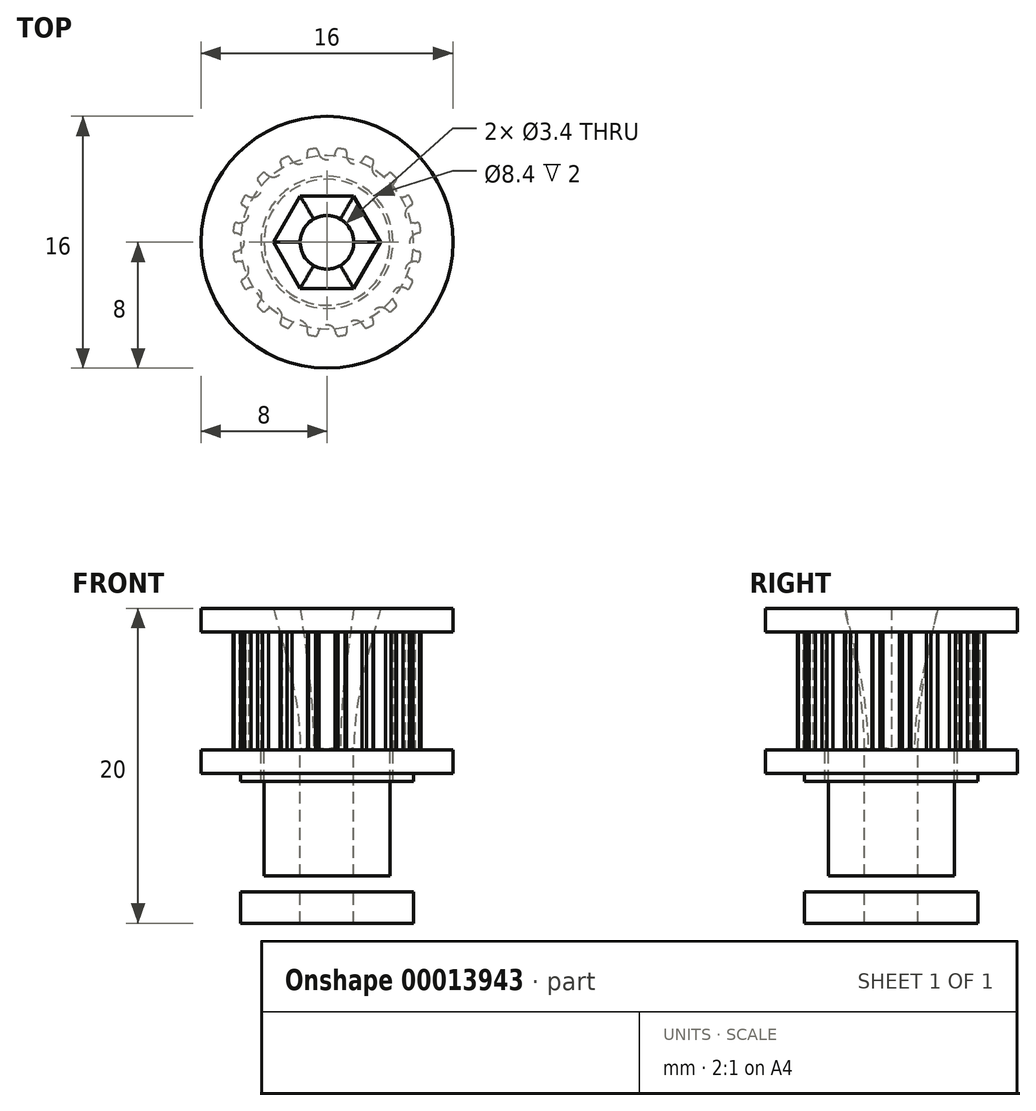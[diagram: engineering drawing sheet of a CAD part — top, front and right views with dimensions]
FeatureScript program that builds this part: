
annotation { "Feature Type Name" : "Feature", "Feature Type Description" : "" }
export const myFeature = defineFeature(function(context is Context, id is Id, definition is map)
    precondition{}
    {
        {
            var Q0;
            Q0=qCreatedBy(makeId("Top.planeOp"),FACE);
            var sketch = newSketch(context, id + "F0", { "sketchPlane" : qUnion([Q0])});
            skLineSegment(sketch, "E0", {"start": v(-19.17, 17.78) * mm, "end": v(-18.17, 17.78) * mm});
            skLineSegment(sketch, "E1", {"start": v(-18.17, 17.78) * mm, "end": v(-18.17, 18.4) * mm});
            skArc(sketch, "E2", {"start": v(-18.67, 18.85) * mm, "mid": v(-18.88, 19.07) * mm, "end": v(-19.17, 19.16) * mm});
            skArc(sketch, "E3", {"start": v(-18.58, 18.54) * mm, "mid": v(-18.61, 18.7) * mm, "end": v(-18.67, 18.85) * mm});
            skArc(sketch, "E4", {"start": v(-18.58, 18.54) * mm, "mid": v(-18.53, 18.44) * mm, "end": v(-18.43, 18.4) * mm});
            skLineSegment(sketch, "E5", {"start": v(-18.43, 18.4) * mm, "end": v(-18.17, 18.4) * mm});
            skArc(sketch, "E6.0.MirrorCS", {"start": v(-19.67, 18.85) * mm, "mid": v(-19.47, 19.07) * mm, "end": v(-19.17, 19.16) * mm});
            skArc(sketch, "E7.0.MirrorCS", {"start": v(-19.76, 18.54) * mm, "mid": v(-19.73, 18.7) * mm, "end": v(-19.67, 18.85) * mm});
            skArc(sketch, "E8.0.MirrorCS", {"start": v(-19.76, 18.54) * mm, "mid": v(-19.81, 18.44) * mm, "end": v(-19.91, 18.4) * mm});
            skLineSegment(sketch, "E9.0.MirrorCS", {"start": v(-19.91, 18.4) * mm, "end": v(-20.17, 18.4) * mm});
            skLineSegment(sketch, "E10.0.MirrorCS", {"start": v(-20.17, 17.78) * mm, "end": v(-20.17, 18.4) * mm});
            skLineSegment(sketch, "E11.0.MirrorCS", {"start": v(-19.17, 17.78) * mm, "end": v(-20.17, 17.78) * mm});
            skLineSegment(sketch, "E12.direction1", {"start": v(-20.17, 17.78) * mm, "end": v(-18.17, 17.78) * mm, "construction": true});
            skLineSegment(sketch, "E13", {"start": v(-20.17, 18.15) * mm, "end": v(-18.17, 18.15) * mm, "construction": true});
            skPoint(sketch, "E14", {"position": v(0, -5.25) * mm});
            skArc(sketch, "E15", {"start": v(0.51, -5.6) * mm, "mid": v(0, -5.25) * mm, "end": v(-0.51, -5.6) * mm});
            skArc(sketch, "E16", {"start": v(-0.51, -5.6) * mm, "mid": v(-0.56, -5.71) * mm, "end": v(-0.59, -5.83) * mm});
            skArc(sketch, "E17", {"start": v(0.59, -5.83) * mm, "mid": v(0.56, -5.71) * mm, "end": v(0.51, -5.6) * mm});
            skArc(sketch, "E18", {"start": v(0.72, -5.96) * mm, "mid": v(0.94, -5.93) * mm, "end": v(1.16, -5.89) * mm});
            skArc(sketch, "E19", {"start": v(0.59, -5.83) * mm, "mid": v(0.66, -5.94) * mm, "end": v(0.8, -5.95) * mm});
            skArc(sketch, "E20", {"start": v(-0.59, -5.83) * mm, "mid": v(-0.66, -5.94) * mm, "end": v(-0.8, -5.95) * mm});
            skArc(sketch, "E21.1.0", {"start": v(2.22, -5.16) * mm, "mid": v(1.62, -5) * mm, "end": v(1.24, -5.48) * mm});
            skPoint(sketch, "E21.1.1", {"position": v(1.62, -5) * mm});
            skArc(sketch, "E21.1.2", {"start": v(1.24, -5.48) * mm, "mid": v(1.23, -5.6) * mm, "end": v(1.24, -5.73) * mm});
            skArc(sketch, "E21.1.3", {"start": v(2.36, -5.37) * mm, "mid": v(2.47, -5.44) * mm, "end": v(2.6, -5.41) * mm});
            skArc(sketch, "E21.1.4", {"start": v(1.24, -5.73) * mm, "mid": v(1.2, -5.85) * mm, "end": v(1.08, -5.9) * mm});
            skArc(sketch, "E21.1.5", {"start": v(2.36, -5.37) * mm, "mid": v(2.3, -5.26) * mm, "end": v(2.22, -5.16) * mm});
            skArc(sketch, "E22.3.2.0", {"start": v(3.7, -4.22) * mm, "mid": v(3.09, -4.25) * mm, "end": v(2.87, -4.83) * mm});
            skPoint(sketch, "E22.4.2.0", {"position": v(3.09, -4.25) * mm});
            skArc(sketch, "E22.5.2.0", {"start": v(2.87, -4.83) * mm, "mid": v(2.9, -4.95) * mm, "end": v(2.95, -5.07) * mm});
            skArc(sketch, "E22.9.2.0", {"start": v(3.9, -4.37) * mm, "mid": v(4.03, -4.41) * mm, "end": v(4.14, -4.35) * mm});
            skArc(sketch, "E22.13.2.0", {"start": v(2.95, -5.07) * mm, "mid": v(2.95, -5.2) * mm, "end": v(2.85, -5.28) * mm});
            skArc(sketch, "E22.17.2.0", {"start": v(3.9, -4.37) * mm, "mid": v(3.81, -4.3) * mm, "end": v(3.7, -4.22) * mm});
            skArc(sketch, "E22.3.3.0", {"start": v(4.83, -2.87) * mm, "mid": v(4.25, -3.09) * mm, "end": v(4.22, -3.7) * mm});
            skPoint(sketch, "E22.4.3.0", {"position": v(4.25, -3.09) * mm});
            skArc(sketch, "E22.5.3.0", {"start": v(4.22, -3.7) * mm, "mid": v(4.3, -3.81) * mm, "end": v(4.37, -3.9) * mm});
            skArc(sketch, "E22.9.3.0", {"start": v(5.07, -2.95) * mm, "mid": v(5.2, -2.95) * mm, "end": v(5.28, -2.85) * mm});
            skArc(sketch, "E22.13.3.0", {"start": v(4.37, -3.9) * mm, "mid": v(4.41, -4.03) * mm, "end": v(4.35, -4.14) * mm});
            skArc(sketch, "E22.17.3.0", {"start": v(5.07, -2.95) * mm, "mid": v(4.95, -2.9) * mm, "end": v(4.83, -2.87) * mm});
            skArc(sketch, "E22.3.4.0", {"start": v(5.48, -1.24) * mm, "mid": v(5, -1.62) * mm, "end": v(5.16, -2.22) * mm});
            skPoint(sketch, "E22.4.4.0", {"position": v(5, -1.62) * mm});
            skArc(sketch, "E22.5.4.0", {"start": v(5.16, -2.22) * mm, "mid": v(5.26, -2.3) * mm, "end": v(5.37, -2.36) * mm});
            skArc(sketch, "E22.9.4.0", {"start": v(5.73, -1.24) * mm, "mid": v(5.85, -1.2) * mm, "end": v(5.9, -1.08) * mm});
            skArc(sketch, "E22.13.4.0", {"start": v(5.37, -2.36) * mm, "mid": v(5.44, -2.47) * mm, "end": v(5.41, -2.6) * mm});
            skArc(sketch, "E22.17.4.0", {"start": v(5.73, -1.24) * mm, "mid": v(5.6, -1.23) * mm, "end": v(5.48, -1.24) * mm});
            skArc(sketch, "E22.3.5.0", {"start": v(5.6, 0.51) * mm, "mid": v(5.25, 0) * mm, "end": v(5.6, -0.51) * mm});
            skPoint(sketch, "E22.4.5.0", {"position": v(5.25, 0) * mm});
            skArc(sketch, "E22.5.5.0", {"start": v(5.6, -0.51) * mm, "mid": v(5.71, -0.56) * mm, "end": v(5.83, -0.59) * mm});
            skArc(sketch, "E22.9.5.0", {"start": v(5.83, 0.59) * mm, "mid": v(5.94, 0.66) * mm, "end": v(5.95, 0.8) * mm});
            skArc(sketch, "E22.13.5.0", {"start": v(5.83, -0.59) * mm, "mid": v(5.94, -0.66) * mm, "end": v(5.95, -0.8) * mm});
            skArc(sketch, "E22.17.5.0", {"start": v(5.83, 0.59) * mm, "mid": v(5.71, 0.56) * mm, "end": v(5.6, 0.51) * mm});
            skArc(sketch, "E22.3.6.0", {"start": v(5.16, 2.22) * mm, "mid": v(5, 1.62) * mm, "end": v(5.48, 1.24) * mm});
            skPoint(sketch, "E22.4.6.0", {"position": v(5, 1.62) * mm});
            skArc(sketch, "E22.5.6.0", {"start": v(5.48, 1.24) * mm, "mid": v(5.6, 1.23) * mm, "end": v(5.73, 1.24) * mm});
            skArc(sketch, "E22.9.6.0", {"start": v(5.37, 2.36) * mm, "mid": v(5.44, 2.47) * mm, "end": v(5.41, 2.6) * mm});
            skArc(sketch, "E22.13.6.0", {"start": v(5.73, 1.24) * mm, "mid": v(5.85, 1.2) * mm, "end": v(5.9, 1.08) * mm});
            skArc(sketch, "E22.17.6.0", {"start": v(5.37, 2.36) * mm, "mid": v(5.26, 2.3) * mm, "end": v(5.16, 2.22) * mm});
            skArc(sketch, "E22.3.7.0", {"start": v(4.22, 3.7) * mm, "mid": v(4.25, 3.09) * mm, "end": v(4.83, 2.87) * mm});
            skPoint(sketch, "E22.4.7.0", {"position": v(4.25, 3.09) * mm});
            skArc(sketch, "E22.5.7.0", {"start": v(4.83, 2.87) * mm, "mid": v(4.95, 2.9) * mm, "end": v(5.07, 2.95) * mm});
            skArc(sketch, "E22.9.7.0", {"start": v(4.37, 3.9) * mm, "mid": v(4.41, 4.03) * mm, "end": v(4.35, 4.14) * mm});
            skArc(sketch, "E22.13.7.0", {"start": v(5.07, 2.95) * mm, "mid": v(5.2, 2.95) * mm, "end": v(5.28, 2.85) * mm});
            skArc(sketch, "E22.17.7.0", {"start": v(4.37, 3.9) * mm, "mid": v(4.3, 3.81) * mm, "end": v(4.22, 3.7) * mm});
            skArc(sketch, "E22.3.8.0", {"start": v(2.87, 4.83) * mm, "mid": v(3.09, 4.25) * mm, "end": v(3.7, 4.22) * mm});
            skPoint(sketch, "E22.4.8.0", {"position": v(3.09, 4.25) * mm});
            skArc(sketch, "E22.5.8.0", {"start": v(3.7, 4.22) * mm, "mid": v(3.81, 4.3) * mm, "end": v(3.9, 4.37) * mm});
            skArc(sketch, "E22.9.8.0", {"start": v(2.95, 5.07) * mm, "mid": v(2.95, 5.2) * mm, "end": v(2.85, 5.28) * mm});
            skArc(sketch, "E22.13.8.0", {"start": v(3.9, 4.37) * mm, "mid": v(4.03, 4.41) * mm, "end": v(4.14, 4.35) * mm});
            skArc(sketch, "E22.17.8.0", {"start": v(2.95, 5.07) * mm, "mid": v(2.9, 4.95) * mm, "end": v(2.87, 4.83) * mm});
            skArc(sketch, "E22.3.9.0", {"start": v(1.24, 5.48) * mm, "mid": v(1.62, 5) * mm, "end": v(2.22, 5.16) * mm});
            skPoint(sketch, "E22.4.9.0", {"position": v(1.62, 5) * mm});
            skArc(sketch, "E22.5.9.0", {"start": v(2.22, 5.16) * mm, "mid": v(2.3, 5.26) * mm, "end": v(2.36, 5.37) * mm});
            skArc(sketch, "E22.9.9.0", {"start": v(1.24, 5.73) * mm, "mid": v(1.2, 5.85) * mm, "end": v(1.08, 5.9) * mm});
            skArc(sketch, "E22.13.9.0", {"start": v(2.36, 5.37) * mm, "mid": v(2.47, 5.44) * mm, "end": v(2.6, 5.41) * mm});
            skArc(sketch, "E22.17.9.0", {"start": v(1.24, 5.73) * mm, "mid": v(1.23, 5.6) * mm, "end": v(1.24, 5.48) * mm});
            skArc(sketch, "E22.3.10.0", {"start": v(-0.51, 5.6) * mm, "mid": v(0, 5.25) * mm, "end": v(0.51, 5.6) * mm});
            skPoint(sketch, "E22.4.10.0", {"position": v(0, 5.25) * mm});
            skArc(sketch, "E22.5.10.0", {"start": v(0.51, 5.6) * mm, "mid": v(0.56, 5.71) * mm, "end": v(0.59, 5.83) * mm});
            skArc(sketch, "E22.9.10.0", {"start": v(-0.59, 5.83) * mm, "mid": v(-0.66, 5.94) * mm, "end": v(-0.8, 5.95) * mm});
            skArc(sketch, "E22.13.10.0", {"start": v(0.59, 5.83) * mm, "mid": v(0.66, 5.94) * mm, "end": v(0.8, 5.95) * mm});
            skArc(sketch, "E22.17.10.0", {"start": v(-0.59, 5.83) * mm, "mid": v(-0.56, 5.71) * mm, "end": v(-0.51, 5.6) * mm});
            skArc(sketch, "E22.3.11.0", {"start": v(-2.22, 5.16) * mm, "mid": v(-1.62, 5) * mm, "end": v(-1.24, 5.48) * mm});
            skPoint(sketch, "E22.4.11.0", {"position": v(-1.62, 5) * mm});
            skArc(sketch, "E22.5.11.0", {"start": v(-1.24, 5.48) * mm, "mid": v(-1.23, 5.6) * mm, "end": v(-1.24, 5.73) * mm});
            skArc(sketch, "E22.9.11.0", {"start": v(-2.36, 5.37) * mm, "mid": v(-2.47, 5.44) * mm, "end": v(-2.6, 5.41) * mm});
            skArc(sketch, "E22.13.11.0", {"start": v(-1.24, 5.73) * mm, "mid": v(-1.2, 5.85) * mm, "end": v(-1.08, 5.9) * mm});
            skArc(sketch, "E22.17.11.0", {"start": v(-2.36, 5.37) * mm, "mid": v(-2.3, 5.26) * mm, "end": v(-2.22, 5.16) * mm});
            skArc(sketch, "E22.3.12.0", {"start": v(-3.7, 4.22) * mm, "mid": v(-3.09, 4.25) * mm, "end": v(-2.87, 4.83) * mm});
            skPoint(sketch, "E22.4.12.0", {"position": v(-3.09, 4.25) * mm});
            skArc(sketch, "E22.5.12.0", {"start": v(-2.87, 4.83) * mm, "mid": v(-2.9, 4.95) * mm, "end": v(-2.95, 5.07) * mm});
            skArc(sketch, "E22.9.12.0", {"start": v(-3.9, 4.37) * mm, "mid": v(-4.03, 4.41) * mm, "end": v(-4.14, 4.35) * mm});
            skArc(sketch, "E22.13.12.0", {"start": v(-2.95, 5.07) * mm, "mid": v(-2.95, 5.2) * mm, "end": v(-2.85, 5.28) * mm});
            skArc(sketch, "E22.17.12.0", {"start": v(-3.9, 4.37) * mm, "mid": v(-3.81, 4.3) * mm, "end": v(-3.7, 4.22) * mm});
            skArc(sketch, "E22.3.13.0", {"start": v(-4.83, 2.87) * mm, "mid": v(-4.25, 3.09) * mm, "end": v(-4.22, 3.7) * mm});
            skPoint(sketch, "E22.4.13.0", {"position": v(-4.25, 3.09) * mm});
            skArc(sketch, "E22.5.13.0", {"start": v(-4.22, 3.7) * mm, "mid": v(-4.3, 3.81) * mm, "end": v(-4.37, 3.9) * mm});
            skArc(sketch, "E22.9.13.0", {"start": v(-5.07, 2.95) * mm, "mid": v(-5.2, 2.95) * mm, "end": v(-5.28, 2.85) * mm});
            skArc(sketch, "E22.13.13.0", {"start": v(-4.37, 3.9) * mm, "mid": v(-4.41, 4.03) * mm, "end": v(-4.35, 4.14) * mm});
            skArc(sketch, "E22.17.13.0", {"start": v(-5.07, 2.95) * mm, "mid": v(-4.95, 2.9) * mm, "end": v(-4.83, 2.87) * mm});
            skArc(sketch, "E22.3.14.0", {"start": v(-5.48, 1.24) * mm, "mid": v(-5, 1.62) * mm, "end": v(-5.16, 2.22) * mm});
            skPoint(sketch, "E22.4.14.0", {"position": v(-5, 1.62) * mm});
            skArc(sketch, "E22.5.14.0", {"start": v(-5.16, 2.22) * mm, "mid": v(-5.26, 2.3) * mm, "end": v(-5.37, 2.36) * mm});
            skArc(sketch, "E22.9.14.0", {"start": v(-5.73, 1.24) * mm, "mid": v(-5.85, 1.2) * mm, "end": v(-5.9, 1.08) * mm});
            skArc(sketch, "E22.13.14.0", {"start": v(-5.37, 2.36) * mm, "mid": v(-5.44, 2.47) * mm, "end": v(-5.41, 2.6) * mm});
            skArc(sketch, "E22.17.14.0", {"start": v(-5.73, 1.24) * mm, "mid": v(-5.6, 1.23) * mm, "end": v(-5.48, 1.24) * mm});
            skArc(sketch, "E22.3.15.0", {"start": v(-5.6, -0.51) * mm, "mid": v(-5.25, 0) * mm, "end": v(-5.6, 0.51) * mm});
            skPoint(sketch, "E22.4.15.0", {"position": v(-5.25, 0) * mm});
            skArc(sketch, "E22.5.15.0", {"start": v(-5.6, 0.51) * mm, "mid": v(-5.71, 0.56) * mm, "end": v(-5.83, 0.59) * mm});
            skArc(sketch, "E22.9.15.0", {"start": v(-5.83, -0.59) * mm, "mid": v(-5.94, -0.66) * mm, "end": v(-5.95, -0.8) * mm});
            skArc(sketch, "E22.13.15.0", {"start": v(-5.83, 0.59) * mm, "mid": v(-5.94, 0.66) * mm, "end": v(-5.95, 0.8) * mm});
            skArc(sketch, "E22.17.15.0", {"start": v(-5.83, -0.59) * mm, "mid": v(-5.71, -0.56) * mm, "end": v(-5.6, -0.51) * mm});
            skArc(sketch, "E22.3.16.0", {"start": v(-5.16, -2.22) * mm, "mid": v(-5, -1.62) * mm, "end": v(-5.48, -1.24) * mm});
            skPoint(sketch, "E22.4.16.0", {"position": v(-5, -1.62) * mm});
            skArc(sketch, "E22.5.16.0", {"start": v(-5.48, -1.24) * mm, "mid": v(-5.6, -1.23) * mm, "end": v(-5.73, -1.24) * mm});
            skArc(sketch, "E22.9.16.0", {"start": v(-5.37, -2.36) * mm, "mid": v(-5.44, -2.47) * mm, "end": v(-5.41, -2.6) * mm});
            skArc(sketch, "E22.13.16.0", {"start": v(-5.73, -1.24) * mm, "mid": v(-5.85, -1.2) * mm, "end": v(-5.9, -1.08) * mm});
            skArc(sketch, "E22.17.16.0", {"start": v(-5.37, -2.36) * mm, "mid": v(-5.26, -2.3) * mm, "end": v(-5.16, -2.22) * mm});
            skArc(sketch, "E22.3.17.0", {"start": v(-4.22, -3.7) * mm, "mid": v(-4.25, -3.09) * mm, "end": v(-4.83, -2.87) * mm});
            skPoint(sketch, "E22.4.17.0", {"position": v(-4.25, -3.09) * mm});
            skArc(sketch, "E22.5.17.0", {"start": v(-4.83, -2.87) * mm, "mid": v(-4.95, -2.9) * mm, "end": v(-5.07, -2.95) * mm});
            skArc(sketch, "E22.9.17.0", {"start": v(-4.37, -3.9) * mm, "mid": v(-4.41, -4.03) * mm, "end": v(-4.35, -4.14) * mm});
            skArc(sketch, "E22.13.17.0", {"start": v(-5.07, -2.95) * mm, "mid": v(-5.2, -2.95) * mm, "end": v(-5.28, -2.85) * mm});
            skArc(sketch, "E22.17.17.0", {"start": v(-4.37, -3.9) * mm, "mid": v(-4.3, -3.81) * mm, "end": v(-4.22, -3.7) * mm});
            skArc(sketch, "E22.3.18.0", {"start": v(-2.87, -4.83) * mm, "mid": v(-3.09, -4.25) * mm, "end": v(-3.7, -4.22) * mm});
            skPoint(sketch, "E22.4.18.0", {"position": v(-3.09, -4.25) * mm});
            skArc(sketch, "E22.5.18.0", {"start": v(-3.7, -4.22) * mm, "mid": v(-3.81, -4.3) * mm, "end": v(-3.9, -4.37) * mm});
            skArc(sketch, "E22.9.18.0", {"start": v(-2.95, -5.07) * mm, "mid": v(-2.95, -5.2) * mm, "end": v(-2.85, -5.28) * mm});
            skArc(sketch, "E22.13.18.0", {"start": v(-3.9, -4.37) * mm, "mid": v(-4.03, -4.41) * mm, "end": v(-4.14, -4.35) * mm});
            skArc(sketch, "E22.17.18.0", {"start": v(-2.95, -5.07) * mm, "mid": v(-2.9, -4.95) * mm, "end": v(-2.87, -4.83) * mm});
            skArc(sketch, "E22.3.19.0", {"start": v(-1.24, -5.48) * mm, "mid": v(-1.62, -5) * mm, "end": v(-2.22, -5.16) * mm});
            skPoint(sketch, "E22.4.19.0", {"position": v(-1.62, -5) * mm});
            skArc(sketch, "E22.5.19.0", {"start": v(-2.22, -5.16) * mm, "mid": v(-2.3, -5.26) * mm, "end": v(-2.36, -5.37) * mm});
            skArc(sketch, "E22.9.19.0", {"start": v(-1.24, -5.73) * mm, "mid": v(-1.2, -5.85) * mm, "end": v(-1.08, -5.9) * mm});
            skArc(sketch, "E22.13.19.0", {"start": v(-2.36, -5.37) * mm, "mid": v(-2.47, -5.44) * mm, "end": v(-2.6, -5.41) * mm});
            skArc(sketch, "E22.17.19.0", {"start": v(-1.24, -5.73) * mm, "mid": v(-1.23, -5.6) * mm, "end": v(-1.24, -5.48) * mm});
            skArc(sketch, "E23.trimOffspring", {"start": v(2.52, -5.44) * mm, "mid": v(2.72, -5.35) * mm, "end": v(2.92, -5.24) * mm});
            skArc(sketch, "E24.trimOffspring", {"start": v(4.08, -4.4) * mm, "mid": v(4.24, -4.24) * mm, "end": v(4.4, -4.08) * mm});
            skArc(sketch, "E25.trimOffspring", {"start": v(5.24, -2.92) * mm, "mid": v(5.33, -2.76) * mm, "end": v(5.41, -2.6) * mm});
            skArc(sketch, "E26.trimOffspring", {"start": v(5.89, -1.16) * mm, "mid": v(5.93, -0.94) * mm, "end": v(5.96, -0.72) * mm});
            skArc(sketch, "E27.trimOffspring", {"start": v(5.44, 2.52) * mm, "mid": v(5.35, 2.72) * mm, "end": v(5.24, 2.92) * mm});
            skArc(sketch, "E28.trimOffspring", {"start": v(4.4, 4.08) * mm, "mid": v(4.24, 4.24) * mm, "end": v(4.08, 4.4) * mm});
            skArc(sketch, "E29.trimOffspring", {"start": v(5.96, 0.72) * mm, "mid": v(5.93, 0.94) * mm, "end": v(5.89, 1.16) * mm});
            skArc(sketch, "E30.trimOffspring", {"start": v(2.92, 5.24) * mm, "mid": v(2.72, 5.35) * mm, "end": v(2.52, 5.44) * mm});
            skArc(sketch, "E31.trimOffspring", {"start": v(1.16, 5.89) * mm, "mid": v(0.94, 5.93) * mm, "end": v(0.72, 5.96) * mm});
            skArc(sketch, "E32.trimOffspring", {"start": v(-0.72, 5.96) * mm, "mid": v(-0.94, 5.93) * mm, "end": v(-1.16, 5.89) * mm});
            skArc(sketch, "E33.trimOffspring", {"start": v(-2.52, 5.44) * mm, "mid": v(-2.72, 5.35) * mm, "end": v(-2.92, 5.24) * mm});
            skArc(sketch, "E34.trimOffspring", {"start": v(-4.08, 4.4) * mm, "mid": v(-4.24, 4.24) * mm, "end": v(-4.4, 4.08) * mm});
            skArc(sketch, "E35.trimOffspring", {"start": v(-5.24, 2.92) * mm, "mid": v(-5.35, 2.72) * mm, "end": v(-5.44, 2.52) * mm});
            skArc(sketch, "E36.trimOffspring", {"start": v(-5.89, 1.16) * mm, "mid": v(-5.93, 0.94) * mm, "end": v(-5.96, 0.72) * mm});
            skArc(sketch, "E37.trimOffspring", {"start": v(-5.96, -0.72) * mm, "mid": v(-5.93, -0.94) * mm, "end": v(-5.89, -1.16) * mm});
            skArc(sketch, "E38.trimOffspring", {"start": v(-5.44, -2.52) * mm, "mid": v(-5.35, -2.72) * mm, "end": v(-5.24, -2.92) * mm});
            skArc(sketch, "E39.trimOffspring", {"start": v(-4.4, -4.08) * mm, "mid": v(-4.24, -4.24) * mm, "end": v(-4.08, -4.4) * mm});
            skArc(sketch, "E40.trimOffspring", {"start": v(-2.92, -5.24) * mm, "mid": v(-2.72, -5.35) * mm, "end": v(-2.52, -5.44) * mm});
            skArc(sketch, "E41.trimOffspring", {"start": v(-1.16, -5.89) * mm, "mid": v(-0.94, -5.93) * mm, "end": v(-0.72, -5.96) * mm});
            skSolve(sketch);
        }
        {
            var Q0;
            Q0=makeQuery(id+"F0.imprint","IMPRINT",FACE,{"disambiguationData":[TD([[makeQuery(id+"F0.imprint","IMPRINT",EDGE,{"derivedFrom":sQuery(id+"F0.wireOp",EDGE,"E15")}),-1.0]])]});
            extrude(context, id + "F1", {"entities" : qUnion([Q0]), "depth" : 7.5 * mm});
        }
        {
            var Q0;
            Q0=makeQuery(id+"F1.opExtrude","CAP_FACE",FACE,{"disambiguationData":[OSD([sQuery(id+"F0.wireOp",EDGE,"E15"),sQuery(id+"F0.wireOp",EDGE,"E16"),sQuery(id+"F0.wireOp",EDGE,"E17"),sQuery(id+"F0.wireOp",EDGE,"E18"),sQuery(id+"F0.wireOp",EDGE,"E19"),sQuery(id+"F0.wireOp",EDGE,"E20"),sQuery(id+"F0.wireOp",EDGE,"E21.1.0"),sQuery(id+"F0.wireOp",EDGE,"E21.1.2"),sQuery(id+"F0.wireOp",EDGE,"E21.1.3"),sQuery(id+"F0.wireOp",EDGE,"E21.1.4"),sQuery(id+"F0.wireOp",EDGE,"E21.1.5"),sQuery(id+"F0.wireOp",EDGE,"E22.3.2.0"),sQuery(id+"F0.wireOp",EDGE,"E22.5.2.0"),sQuery(id+"F0.wireOp",EDGE,"E22.9.2.0"),sQuery(id+"F0.wireOp",EDGE,"E22.13.2.0"),sQuery(id+"F0.wireOp",EDGE,"E22.17.2.0"),sQuery(id+"F0.wireOp",EDGE,"E22.3.3.0"),sQuery(id+"F0.wireOp",EDGE,"E22.5.3.0"),sQuery(id+"F0.wireOp",EDGE,"E22.9.3.0"),sQuery(id+"F0.wireOp",EDGE,"E22.13.3.0"),sQuery(id+"F0.wireOp",EDGE,"E22.17.3.0"),sQuery(id+"F0.wireOp",EDGE,"E22.3.4.0"),sQuery(id+"F0.wireOp",EDGE,"E22.5.4.0"),sQuery(id+"F0.wireOp",EDGE,"E22.9.4.0"),sQuery(id+"F0.wireOp",EDGE,"E22.13.4.0"),sQuery(id+"F0.wireOp",EDGE,"E22.17.4.0"),sQuery(id+"F0.wireOp",EDGE,"E22.3.5.0"),sQuery(id+"F0.wireOp",EDGE,"E22.5.5.0"),sQuery(id+"F0.wireOp",EDGE,"E22.9.5.0"),sQuery(id+"F0.wireOp",EDGE,"E22.13.5.0"),sQuery(id+"F0.wireOp",EDGE,"E22.17.5.0"),sQuery(id+"F0.wireOp",EDGE,"E22.3.6.0"),sQuery(id+"F0.wireOp",EDGE,"E22.5.6.0"),sQuery(id+"F0.wireOp",EDGE,"E22.9.6.0"),sQuery(id+"F0.wireOp",EDGE,"E22.13.6.0"),sQuery(id+"F0.wireOp",EDGE,"E22.17.6.0"),sQuery(id+"F0.wireOp",EDGE,"E22.3.7.0"),sQuery(id+"F0.wireOp",EDGE,"E22.5.7.0"),sQuery(id+"F0.wireOp",EDGE,"E22.9.7.0"),sQuery(id+"F0.wireOp",EDGE,"E22.13.7.0"),sQuery(id+"F0.wireOp",EDGE,"E22.17.7.0"),sQuery(id+"F0.wireOp",EDGE,"E22.3.8.0"),sQuery(id+"F0.wireOp",EDGE,"E22.5.8.0"),sQuery(id+"F0.wireOp",EDGE,"E22.9.8.0"),sQuery(id+"F0.wireOp",EDGE,"E22.13.8.0"),sQuery(id+"F0.wireOp",EDGE,"E22.17.8.0"),sQuery(id+"F0.wireOp",EDGE,"E22.3.9.0"),sQuery(id+"F0.wireOp",EDGE,"E22.5.9.0"),sQuery(id+"F0.wireOp",EDGE,"E22.9.9.0"),sQuery(id+"F0.wireOp",EDGE,"E22.13.9.0"),sQuery(id+"F0.wireOp",EDGE,"E22.17.9.0"),sQuery(id+"F0.wireOp",EDGE,"E22.3.10.0"),sQuery(id+"F0.wireOp",EDGE,"E22.5.10.0"),sQuery(id+"F0.wireOp",EDGE,"E22.9.10.0"),sQuery(id+"F0.wireOp",EDGE,"E22.13.10.0"),sQuery(id+"F0.wireOp",EDGE,"E22.17.10.0"),sQuery(id+"F0.wireOp",EDGE,"E22.3.11.0"),sQuery(id+"F0.wireOp",EDGE,"E22.5.11.0"),sQuery(id+"F0.wireOp",EDGE,"E22.9.11.0"),sQuery(id+"F0.wireOp",EDGE,"E22.13.11.0"),sQuery(id+"F0.wireOp",EDGE,"E22.17.11.0"),sQuery(id+"F0.wireOp",EDGE,"E22.3.12.0"),sQuery(id+"F0.wireOp",EDGE,"E22.5.12.0"),sQuery(id+"F0.wireOp",EDGE,"E22.9.12.0"),sQuery(id+"F0.wireOp",EDGE,"E22.13.12.0"),sQuery(id+"F0.wireOp",EDGE,"E22.17.12.0"),sQuery(id+"F0.wireOp",EDGE,"E22.3.13.0"),sQuery(id+"F0.wireOp",EDGE,"E22.5.13.0"),sQuery(id+"F0.wireOp",EDGE,"E22.9.13.0"),sQuery(id+"F0.wireOp",EDGE,"E22.13.13.0"),sQuery(id+"F0.wireOp",EDGE,"E22.17.13.0"),sQuery(id+"F0.wireOp",EDGE,"E22.3.14.0"),sQuery(id+"F0.wireOp",EDGE,"E22.5.14.0"),sQuery(id+"F0.wireOp",EDGE,"E22.9.14.0"),sQuery(id+"F0.wireOp",EDGE,"E22.13.14.0"),sQuery(id+"F0.wireOp",EDGE,"E22.17.14.0"),sQuery(id+"F0.wireOp",EDGE,"E22.3.15.0"),sQuery(id+"F0.wireOp",EDGE,"E22.5.15.0"),sQuery(id+"F0.wireOp",EDGE,"E22.9.15.0"),sQuery(id+"F0.wireOp",EDGE,"E22.13.15.0"),sQuery(id+"F0.wireOp",EDGE,"E22.17.15.0"),sQuery(id+"F0.wireOp",EDGE,"E22.3.16.0"),sQuery(id+"F0.wireOp",EDGE,"E22.5.16.0"),sQuery(id+"F0.wireOp",EDGE,"E22.9.16.0"),sQuery(id+"F0.wireOp",EDGE,"E22.13.16.0"),sQuery(id+"F0.wireOp",EDGE,"E22.17.16.0"),sQuery(id+"F0.wireOp",EDGE,"E22.3.17.0"),sQuery(id+"F0.wireOp",EDGE,"E22.5.17.0"),sQuery(id+"F0.wireOp",EDGE,"E22.9.17.0"),sQuery(id+"F0.wireOp",EDGE,"E22.13.17.0"),sQuery(id+"F0.wireOp",EDGE,"E22.17.17.0"),sQuery(id+"F0.wireOp",EDGE,"E22.3.18.0"),sQuery(id+"F0.wireOp",EDGE,"E22.5.18.0"),sQuery(id+"F0.wireOp",EDGE,"E22.9.18.0"),sQuery(id+"F0.wireOp",EDGE,"E22.13.18.0"),sQuery(id+"F0.wireOp",EDGE,"E22.17.18.0"),sQuery(id+"F0.wireOp",EDGE,"E22.3.19.0"),sQuery(id+"F0.wireOp",EDGE,"E22.5.19.0"),sQuery(id+"F0.wireOp",EDGE,"E22.9.19.0"),sQuery(id+"F0.wireOp",EDGE,"E22.13.19.0"),sQuery(id+"F0.wireOp",EDGE,"E22.17.19.0"),sQuery(id+"F0.wireOp",EDGE,"E23.trimOffspring"),sQuery(id+"F0.wireOp",EDGE,"E24.trimOffspring"),sQuery(id+"F0.wireOp",EDGE,"E25.trimOffspring"),sQuery(id+"F0.wireOp",EDGE,"E26.trimOffspring"),sQuery(id+"F0.wireOp",EDGE,"E27.trimOffspring"),sQuery(id+"F0.wireOp",EDGE,"E28.trimOffspring"),sQuery(id+"F0.wireOp",EDGE,"E29.trimOffspring"),sQuery(id+"F0.wireOp",EDGE,"E30.trimOffspring"),sQuery(id+"F0.wireOp",EDGE,"E31.trimOffspring"),sQuery(id+"F0.wireOp",EDGE,"E32.trimOffspring"),sQuery(id+"F0.wireOp",EDGE,"E33.trimOffspring"),sQuery(id+"F0.wireOp",EDGE,"E34.trimOffspring"),sQuery(id+"F0.wireOp",EDGE,"E35.trimOffspring"),sQuery(id+"F0.wireOp",EDGE,"E36.trimOffspring"),sQuery(id+"F0.wireOp",EDGE,"E37.trimOffspring"),sQuery(id+"F0.wireOp",EDGE,"E38.trimOffspring"),sQuery(id+"F0.wireOp",EDGE,"E39.trimOffspring"),sQuery(id+"F0.wireOp",EDGE,"E40.trimOffspring"),sQuery(id+"F0.wireOp",EDGE,"E41.trimOffspring")])],"isStart":false});
            var sketch = newSketch(context, id + "F2", { "sketchPlane" : qUnion([Q0])});
            skCircle(sketch, "E42", {"center": v(0, 0) * mm, "radius": 8 * mm});
            skSolve(sketch);
        }
        {
            var Q0;
            Q0=qSketchRegion(id+"F2",true);
            extrude(context, id + "F3", {"entities" : qUnion([Q0]), "operationType" : NewBodyOperationType.ADD, "depth" : 1.5 * mm});
        }
        {
            var Q0;
            Q0=makeQuery(id+"F1.opExtrude","CAP_FACE",FACE,{"disambiguationData":[OSD([sQuery(id+"F0.wireOp",EDGE,"E15"),sQuery(id+"F0.wireOp",EDGE,"E16"),sQuery(id+"F0.wireOp",EDGE,"E17"),sQuery(id+"F0.wireOp",EDGE,"E18"),sQuery(id+"F0.wireOp",EDGE,"E19"),sQuery(id+"F0.wireOp",EDGE,"E20"),sQuery(id+"F0.wireOp",EDGE,"E21.1.0"),sQuery(id+"F0.wireOp",EDGE,"E21.1.2"),sQuery(id+"F0.wireOp",EDGE,"E21.1.3"),sQuery(id+"F0.wireOp",EDGE,"E21.1.4"),sQuery(id+"F0.wireOp",EDGE,"E21.1.5"),sQuery(id+"F0.wireOp",EDGE,"E22.3.2.0"),sQuery(id+"F0.wireOp",EDGE,"E22.5.2.0"),sQuery(id+"F0.wireOp",EDGE,"E22.9.2.0"),sQuery(id+"F0.wireOp",EDGE,"E22.13.2.0"),sQuery(id+"F0.wireOp",EDGE,"E22.17.2.0"),sQuery(id+"F0.wireOp",EDGE,"E22.3.3.0"),sQuery(id+"F0.wireOp",EDGE,"E22.5.3.0"),sQuery(id+"F0.wireOp",EDGE,"E22.9.3.0"),sQuery(id+"F0.wireOp",EDGE,"E22.13.3.0"),sQuery(id+"F0.wireOp",EDGE,"E22.17.3.0"),sQuery(id+"F0.wireOp",EDGE,"E22.3.4.0"),sQuery(id+"F0.wireOp",EDGE,"E22.5.4.0"),sQuery(id+"F0.wireOp",EDGE,"E22.9.4.0"),sQuery(id+"F0.wireOp",EDGE,"E22.13.4.0"),sQuery(id+"F0.wireOp",EDGE,"E22.17.4.0"),sQuery(id+"F0.wireOp",EDGE,"E22.3.5.0"),sQuery(id+"F0.wireOp",EDGE,"E22.5.5.0"),sQuery(id+"F0.wireOp",EDGE,"E22.9.5.0"),sQuery(id+"F0.wireOp",EDGE,"E22.13.5.0"),sQuery(id+"F0.wireOp",EDGE,"E22.17.5.0"),sQuery(id+"F0.wireOp",EDGE,"E22.3.6.0"),sQuery(id+"F0.wireOp",EDGE,"E22.5.6.0"),sQuery(id+"F0.wireOp",EDGE,"E22.9.6.0"),sQuery(id+"F0.wireOp",EDGE,"E22.13.6.0"),sQuery(id+"F0.wireOp",EDGE,"E22.17.6.0"),sQuery(id+"F0.wireOp",EDGE,"E22.3.7.0"),sQuery(id+"F0.wireOp",EDGE,"E22.5.7.0"),sQuery(id+"F0.wireOp",EDGE,"E22.9.7.0"),sQuery(id+"F0.wireOp",EDGE,"E22.13.7.0"),sQuery(id+"F0.wireOp",EDGE,"E22.17.7.0"),sQuery(id+"F0.wireOp",EDGE,"E22.3.8.0"),sQuery(id+"F0.wireOp",EDGE,"E22.5.8.0"),sQuery(id+"F0.wireOp",EDGE,"E22.9.8.0"),sQuery(id+"F0.wireOp",EDGE,"E22.13.8.0"),sQuery(id+"F0.wireOp",EDGE,"E22.17.8.0"),sQuery(id+"F0.wireOp",EDGE,"E22.3.9.0"),sQuery(id+"F0.wireOp",EDGE,"E22.5.9.0"),sQuery(id+"F0.wireOp",EDGE,"E22.9.9.0"),sQuery(id+"F0.wireOp",EDGE,"E22.13.9.0"),sQuery(id+"F0.wireOp",EDGE,"E22.17.9.0"),sQuery(id+"F0.wireOp",EDGE,"E22.3.10.0"),sQuery(id+"F0.wireOp",EDGE,"E22.5.10.0"),sQuery(id+"F0.wireOp",EDGE,"E22.9.10.0"),sQuery(id+"F0.wireOp",EDGE,"E22.13.10.0"),sQuery(id+"F0.wireOp",EDGE,"E22.17.10.0"),sQuery(id+"F0.wireOp",EDGE,"E22.3.11.0"),sQuery(id+"F0.wireOp",EDGE,"E22.5.11.0"),sQuery(id+"F0.wireOp",EDGE,"E22.9.11.0"),sQuery(id+"F0.wireOp",EDGE,"E22.13.11.0"),sQuery(id+"F0.wireOp",EDGE,"E22.17.11.0"),sQuery(id+"F0.wireOp",EDGE,"E22.3.12.0"),sQuery(id+"F0.wireOp",EDGE,"E22.5.12.0"),sQuery(id+"F0.wireOp",EDGE,"E22.9.12.0"),sQuery(id+"F0.wireOp",EDGE,"E22.13.12.0"),sQuery(id+"F0.wireOp",EDGE,"E22.17.12.0"),sQuery(id+"F0.wireOp",EDGE,"E22.3.13.0"),sQuery(id+"F0.wireOp",EDGE,"E22.5.13.0"),sQuery(id+"F0.wireOp",EDGE,"E22.9.13.0"),sQuery(id+"F0.wireOp",EDGE,"E22.13.13.0"),sQuery(id+"F0.wireOp",EDGE,"E22.17.13.0"),sQuery(id+"F0.wireOp",EDGE,"E22.3.14.0"),sQuery(id+"F0.wireOp",EDGE,"E22.5.14.0"),sQuery(id+"F0.wireOp",EDGE,"E22.9.14.0"),sQuery(id+"F0.wireOp",EDGE,"E22.13.14.0"),sQuery(id+"F0.wireOp",EDGE,"E22.17.14.0"),sQuery(id+"F0.wireOp",EDGE,"E22.3.15.0"),sQuery(id+"F0.wireOp",EDGE,"E22.5.15.0"),sQuery(id+"F0.wireOp",EDGE,"E22.9.15.0"),sQuery(id+"F0.wireOp",EDGE,"E22.13.15.0"),sQuery(id+"F0.wireOp",EDGE,"E22.17.15.0"),sQuery(id+"F0.wireOp",EDGE,"E22.3.16.0"),sQuery(id+"F0.wireOp",EDGE,"E22.5.16.0"),sQuery(id+"F0.wireOp",EDGE,"E22.9.16.0"),sQuery(id+"F0.wireOp",EDGE,"E22.13.16.0"),sQuery(id+"F0.wireOp",EDGE,"E22.17.16.0"),sQuery(id+"F0.wireOp",EDGE,"E22.3.17.0"),sQuery(id+"F0.wireOp",EDGE,"E22.5.17.0"),sQuery(id+"F0.wireOp",EDGE,"E22.9.17.0"),sQuery(id+"F0.wireOp",EDGE,"E22.13.17.0"),sQuery(id+"F0.wireOp",EDGE,"E22.17.17.0"),sQuery(id+"F0.wireOp",EDGE,"E22.3.18.0"),sQuery(id+"F0.wireOp",EDGE,"E22.5.18.0"),sQuery(id+"F0.wireOp",EDGE,"E22.9.18.0"),sQuery(id+"F0.wireOp",EDGE,"E22.13.18.0"),sQuery(id+"F0.wireOp",EDGE,"E22.17.18.0"),sQuery(id+"F0.wireOp",EDGE,"E22.3.19.0"),sQuery(id+"F0.wireOp",EDGE,"E22.5.19.0"),sQuery(id+"F0.wireOp",EDGE,"E22.9.19.0"),sQuery(id+"F0.wireOp",EDGE,"E22.13.19.0"),sQuery(id+"F0.wireOp",EDGE,"E22.17.19.0"),sQuery(id+"F0.wireOp",EDGE,"E23.trimOffspring"),sQuery(id+"F0.wireOp",EDGE,"E24.trimOffspring"),sQuery(id+"F0.wireOp",EDGE,"E25.trimOffspring"),sQuery(id+"F0.wireOp",EDGE,"E26.trimOffspring"),sQuery(id+"F0.wireOp",EDGE,"E27.trimOffspring"),sQuery(id+"F0.wireOp",EDGE,"E28.trimOffspring"),sQuery(id+"F0.wireOp",EDGE,"E29.trimOffspring"),sQuery(id+"F0.wireOp",EDGE,"E30.trimOffspring"),sQuery(id+"F0.wireOp",EDGE,"E31.trimOffspring"),sQuery(id+"F0.wireOp",EDGE,"E32.trimOffspring"),sQuery(id+"F0.wireOp",EDGE,"E33.trimOffspring"),sQuery(id+"F0.wireOp",EDGE,"E34.trimOffspring"),sQuery(id+"F0.wireOp",EDGE,"E35.trimOffspring"),sQuery(id+"F0.wireOp",EDGE,"E36.trimOffspring"),sQuery(id+"F0.wireOp",EDGE,"E37.trimOffspring"),sQuery(id+"F0.wireOp",EDGE,"E38.trimOffspring"),sQuery(id+"F0.wireOp",EDGE,"E39.trimOffspring"),sQuery(id+"F0.wireOp",EDGE,"E40.trimOffspring"),sQuery(id+"F0.wireOp",EDGE,"E41.trimOffspring")])],"isStart":true});
            var sketch = newSketch(context, id + "F4", { "sketchPlane" : qUnion([Q0])});
            skCircle(sketch, "E43.0", {"center": v(0, 0) * mm, "radius": 8 * mm});
            skCircle(sketch, "E44", {"center": v(0, 0) * mm, "radius": 4.2 * mm});
            skSolve(sketch);
        }
        {
            var Q0;
            Q0=qSketchRegion(id+"F4",true);
            extrude(context, id + "F5", {"entities" : qUnion([Q0]), "depth" : 1.5 * mm});
        }
        {
            var Q0;
            Q0=makeQuery(id+"F3.opExtrude","CAP_FACE",FACE,{"disambiguationData":[OSD([sQuery(id+"F2.wireOp",EDGE,"E42")])],"isStart":false});
            var sketch = newSketch(context, id + "F6", { "sketchPlane" : qUnion([Q0])});
            skCircle(sketch, "E45.cCircle", {"center": v(0, 0) * mm, "radius": 2.95 * mm, "construction": true});
            skLineSegment(sketch, "E45.0", {"start": v(3.4, 0) * mm, "end": v(1.7, -2.95) * mm});
            skLineSegment(sketch, "E45.1", {"start": v(1.7, -2.95) * mm, "end": v(-1.7, -2.95) * mm});
            skLineSegment(sketch, "E45.2", {"start": v(-1.7, -2.95) * mm, "end": v(-3.4, 0) * mm});
            skLineSegment(sketch, "E45.3", {"start": v(-3.4, 0) * mm, "end": v(-1.7, 2.95) * mm});
            skLineSegment(sketch, "E45.4", {"start": v(-1.7, 2.95) * mm, "end": v(1.7, 2.95) * mm});
            skLineSegment(sketch, "E45.5", {"start": v(1.7, 2.95) * mm, "end": v(3.4, 0) * mm});
            skPoint(sketch, "E45.0.midPoint", {"position": v(2.55, -1.48) * mm});
            skSolve(sketch);
        }
        {
            var Q0;
            Q0=makeQuery(id+"F5.opExtrude","CAP_FACE",FACE,{"disambiguationData":[OSD([sQuery(id+"F4.wireOp",EDGE,"E43.0")])],"isStart":false});
            var sketch = newSketch(context, id + "F7", { "sketchPlane" : qUnion([Q0])});
            skCircle(sketch, "E46", {"center": v(0, 0) * mm, "radius": 5.5 * mm});
            skCircle(sketch, "E47", {"center": v(0, 0) * mm, "radius": 4.2 * mm});
            skSolve(sketch);
        }
        {
            var Q0;
            Q0=makeQuery(id+"F7.imprint","IMPRINT",FACE,{"disambiguationData":[TD([[makeQuery(id+"F7.imprint","IMPRINT",EDGE,{"derivedFrom":sQuery(id+"F7.wireOp",EDGE,"E46")}),1.0]])]});
            extrude(context, id + "F8", {"entities" : qUnion([Q0]), "operationType" : NewBodyOperationType.ADD, "depth" : 0.5 * mm});
        }
        {
            var Q0;
            Q0=makeQuery(id+"F1.opExtrude","CAP_FACE",FACE,{"disambiguationData":[OSD([sQuery(id+"F0.wireOp",EDGE,"E15"),sQuery(id+"F0.wireOp",EDGE,"E16"),sQuery(id+"F0.wireOp",EDGE,"E17"),sQuery(id+"F0.wireOp",EDGE,"E18"),sQuery(id+"F0.wireOp",EDGE,"E19"),sQuery(id+"F0.wireOp",EDGE,"E20"),sQuery(id+"F0.wireOp",EDGE,"E21.1.0"),sQuery(id+"F0.wireOp",EDGE,"E21.1.2"),sQuery(id+"F0.wireOp",EDGE,"E21.1.3"),sQuery(id+"F0.wireOp",EDGE,"E21.1.4"),sQuery(id+"F0.wireOp",EDGE,"E21.1.5"),sQuery(id+"F0.wireOp",EDGE,"E22.3.2.0"),sQuery(id+"F0.wireOp",EDGE,"E22.5.2.0"),sQuery(id+"F0.wireOp",EDGE,"E22.9.2.0"),sQuery(id+"F0.wireOp",EDGE,"E22.13.2.0"),sQuery(id+"F0.wireOp",EDGE,"E22.17.2.0"),sQuery(id+"F0.wireOp",EDGE,"E22.3.3.0"),sQuery(id+"F0.wireOp",EDGE,"E22.5.3.0"),sQuery(id+"F0.wireOp",EDGE,"E22.9.3.0"),sQuery(id+"F0.wireOp",EDGE,"E22.13.3.0"),sQuery(id+"F0.wireOp",EDGE,"E22.17.3.0"),sQuery(id+"F0.wireOp",EDGE,"E22.3.4.0"),sQuery(id+"F0.wireOp",EDGE,"E22.5.4.0"),sQuery(id+"F0.wireOp",EDGE,"E22.9.4.0"),sQuery(id+"F0.wireOp",EDGE,"E22.13.4.0"),sQuery(id+"F0.wireOp",EDGE,"E22.17.4.0"),sQuery(id+"F0.wireOp",EDGE,"E22.3.5.0"),sQuery(id+"F0.wireOp",EDGE,"E22.5.5.0"),sQuery(id+"F0.wireOp",EDGE,"E22.9.5.0"),sQuery(id+"F0.wireOp",EDGE,"E22.13.5.0"),sQuery(id+"F0.wireOp",EDGE,"E22.17.5.0"),sQuery(id+"F0.wireOp",EDGE,"E22.3.6.0"),sQuery(id+"F0.wireOp",EDGE,"E22.5.6.0"),sQuery(id+"F0.wireOp",EDGE,"E22.9.6.0"),sQuery(id+"F0.wireOp",EDGE,"E22.13.6.0"),sQuery(id+"F0.wireOp",EDGE,"E22.17.6.0"),sQuery(id+"F0.wireOp",EDGE,"E22.3.7.0"),sQuery(id+"F0.wireOp",EDGE,"E22.5.7.0"),sQuery(id+"F0.wireOp",EDGE,"E22.9.7.0"),sQuery(id+"F0.wireOp",EDGE,"E22.13.7.0"),sQuery(id+"F0.wireOp",EDGE,"E22.17.7.0"),sQuery(id+"F0.wireOp",EDGE,"E22.3.8.0"),sQuery(id+"F0.wireOp",EDGE,"E22.5.8.0"),sQuery(id+"F0.wireOp",EDGE,"E22.9.8.0"),sQuery(id+"F0.wireOp",EDGE,"E22.13.8.0"),sQuery(id+"F0.wireOp",EDGE,"E22.17.8.0"),sQuery(id+"F0.wireOp",EDGE,"E22.3.9.0"),sQuery(id+"F0.wireOp",EDGE,"E22.5.9.0"),sQuery(id+"F0.wireOp",EDGE,"E22.9.9.0"),sQuery(id+"F0.wireOp",EDGE,"E22.13.9.0"),sQuery(id+"F0.wireOp",EDGE,"E22.17.9.0"),sQuery(id+"F0.wireOp",EDGE,"E22.3.10.0"),sQuery(id+"F0.wireOp",EDGE,"E22.5.10.0"),sQuery(id+"F0.wireOp",EDGE,"E22.9.10.0"),sQuery(id+"F0.wireOp",EDGE,"E22.13.10.0"),sQuery(id+"F0.wireOp",EDGE,"E22.17.10.0"),sQuery(id+"F0.wireOp",EDGE,"E22.3.11.0"),sQuery(id+"F0.wireOp",EDGE,"E22.5.11.0"),sQuery(id+"F0.wireOp",EDGE,"E22.9.11.0"),sQuery(id+"F0.wireOp",EDGE,"E22.13.11.0"),sQuery(id+"F0.wireOp",EDGE,"E22.17.11.0"),sQuery(id+"F0.wireOp",EDGE,"E22.3.12.0"),sQuery(id+"F0.wireOp",EDGE,"E22.5.12.0"),sQuery(id+"F0.wireOp",EDGE,"E22.9.12.0"),sQuery(id+"F0.wireOp",EDGE,"E22.13.12.0"),sQuery(id+"F0.wireOp",EDGE,"E22.17.12.0"),sQuery(id+"F0.wireOp",EDGE,"E22.3.13.0"),sQuery(id+"F0.wireOp",EDGE,"E22.5.13.0"),sQuery(id+"F0.wireOp",EDGE,"E22.9.13.0"),sQuery(id+"F0.wireOp",EDGE,"E22.13.13.0"),sQuery(id+"F0.wireOp",EDGE,"E22.17.13.0"),sQuery(id+"F0.wireOp",EDGE,"E22.3.14.0"),sQuery(id+"F0.wireOp",EDGE,"E22.5.14.0"),sQuery(id+"F0.wireOp",EDGE,"E22.9.14.0"),sQuery(id+"F0.wireOp",EDGE,"E22.13.14.0"),sQuery(id+"F0.wireOp",EDGE,"E22.17.14.0"),sQuery(id+"F0.wireOp",EDGE,"E22.3.15.0"),sQuery(id+"F0.wireOp",EDGE,"E22.5.15.0"),sQuery(id+"F0.wireOp",EDGE,"E22.9.15.0"),sQuery(id+"F0.wireOp",EDGE,"E22.13.15.0"),sQuery(id+"F0.wireOp",EDGE,"E22.17.15.0"),sQuery(id+"F0.wireOp",EDGE,"E22.3.16.0"),sQuery(id+"F0.wireOp",EDGE,"E22.5.16.0"),sQuery(id+"F0.wireOp",EDGE,"E22.9.16.0"),sQuery(id+"F0.wireOp",EDGE,"E22.13.16.0"),sQuery(id+"F0.wireOp",EDGE,"E22.17.16.0"),sQuery(id+"F0.wireOp",EDGE,"E22.3.17.0"),sQuery(id+"F0.wireOp",EDGE,"E22.5.17.0"),sQuery(id+"F0.wireOp",EDGE,"E22.9.17.0"),sQuery(id+"F0.wireOp",EDGE,"E22.13.17.0"),sQuery(id+"F0.wireOp",EDGE,"E22.17.17.0"),sQuery(id+"F0.wireOp",EDGE,"E22.3.18.0"),sQuery(id+"F0.wireOp",EDGE,"E22.5.18.0"),sQuery(id+"F0.wireOp",EDGE,"E22.9.18.0"),sQuery(id+"F0.wireOp",EDGE,"E22.13.18.0"),sQuery(id+"F0.wireOp",EDGE,"E22.17.18.0"),sQuery(id+"F0.wireOp",EDGE,"E22.3.19.0"),sQuery(id+"F0.wireOp",EDGE,"E22.5.19.0"),sQuery(id+"F0.wireOp",EDGE,"E22.9.19.0"),sQuery(id+"F0.wireOp",EDGE,"E22.13.19.0"),sQuery(id+"F0.wireOp",EDGE,"E22.17.19.0"),sQuery(id+"F0.wireOp",EDGE,"E23.trimOffspring"),sQuery(id+"F0.wireOp",EDGE,"E24.trimOffspring"),sQuery(id+"F0.wireOp",EDGE,"E25.trimOffspring"),sQuery(id+"F0.wireOp",EDGE,"E26.trimOffspring"),sQuery(id+"F0.wireOp",EDGE,"E27.trimOffspring"),sQuery(id+"F0.wireOp",EDGE,"E28.trimOffspring"),sQuery(id+"F0.wireOp",EDGE,"E29.trimOffspring"),sQuery(id+"F0.wireOp",EDGE,"E30.trimOffspring"),sQuery(id+"F0.wireOp",EDGE,"E31.trimOffspring"),sQuery(id+"F0.wireOp",EDGE,"E32.trimOffspring"),sQuery(id+"F0.wireOp",EDGE,"E33.trimOffspring"),sQuery(id+"F0.wireOp",EDGE,"E34.trimOffspring"),sQuery(id+"F0.wireOp",EDGE,"E35.trimOffspring"),sQuery(id+"F0.wireOp",EDGE,"E36.trimOffspring"),sQuery(id+"F0.wireOp",EDGE,"E37.trimOffspring"),sQuery(id+"F0.wireOp",EDGE,"E38.trimOffspring"),sQuery(id+"F0.wireOp",EDGE,"E39.trimOffspring"),sQuery(id+"F0.wireOp",EDGE,"E40.trimOffspring"),sQuery(id+"F0.wireOp",EDGE,"E41.trimOffspring")])],"isStart":true});
            var sketch = newSketch(context, id + "F9", { "sketchPlane" : qUnion([Q0])});
            skCircle(sketch, "E48", {"center": v(0, 0) * mm, "radius": 4 * mm});
            skSolve(sketch);
        }
        {
            var Q0;
            Q0 = qSketchRegion(id + "F9", true);
            extrude(context, id + "F10", {"entities" : qUnion([Q0]), "operationType" : NewBodyOperationType.ADD, "depth" : 8 * mm});
        }
        {
            var Q0;
            Q0=qCreatedBy(makeId("Top.planeOp"),FACE);
            var sketch = newSketch(context, id + "F11", { "sketchPlane" : qUnion([Q0])});
            skCircle(sketch, "E49", {"center": v(0, 0) * mm, "radius": 1.7 * mm});
            skSolve(sketch);
        }
        {
            var Q0;
            Q0 = qSketchRegion(id + "F11", true);
            extrude(context, id + "F12", {"entities" : qUnion([Q0]), "operationType" : NewBodyOperationType.REMOVE, "endBound" : BoundingType.SYMMETRIC, "oppositeDirection" : true, "depth" : 25 * mm});
        }
        {
            var Q1;
            Q1 = qSketchRegion(id + "F6", true);
            var Q2;
            Q2 = qSketchRegion(id + "F11", true);
            loft(context, id + "F13", {"operationType" : NewBodyOperationType.REMOVE, "endCondition" : LoftEndDerivativeType.NORMAL_TO_PROFILE, "endMagnitude" : 1, "sheetProfilesArray" : [{ "sheetProfileEntities" : qUnion([Q1]) }, { "sheetProfileEntities" : qUnion([Q2]) }]});
        }
        {
            var Q0;
            Q0=qCreatedBy(makeId("Top.planeOp"),FACE);
            cPlane(context, id + "F14", {"entities" : qUnion([Q0]), "cplaneType" : CPlaneType.OFFSET, "offset" : 9 * mm, "oppositeDirection" : true, "width" : 150 * mm, "height" : 150 * mm});
        }
        {
            var Q0;
            Q0=qCreatedBy(id+"F14.planeOp",FACE);
            var sketch = newSketch(context, id + "F15", { "sketchPlane" : qUnion([Q0])});
            skCircle(sketch, "E50.0", {"center": v(0, 0) * mm, "radius": 1.7 * mm});
            skCircle(sketch, "E51.0", {"center": v(0, 0) * mm, "radius": 5.5 * mm});
            skSolve(sketch);
        }
        {
            var Q0;
            Q0 = qSketchRegion(id + "F15", true);
            extrude(context, id + "F16", {"entities" : qUnion([Q0]), "oppositeDirection" : true, "depth" : 2 * mm});
        }
    });
